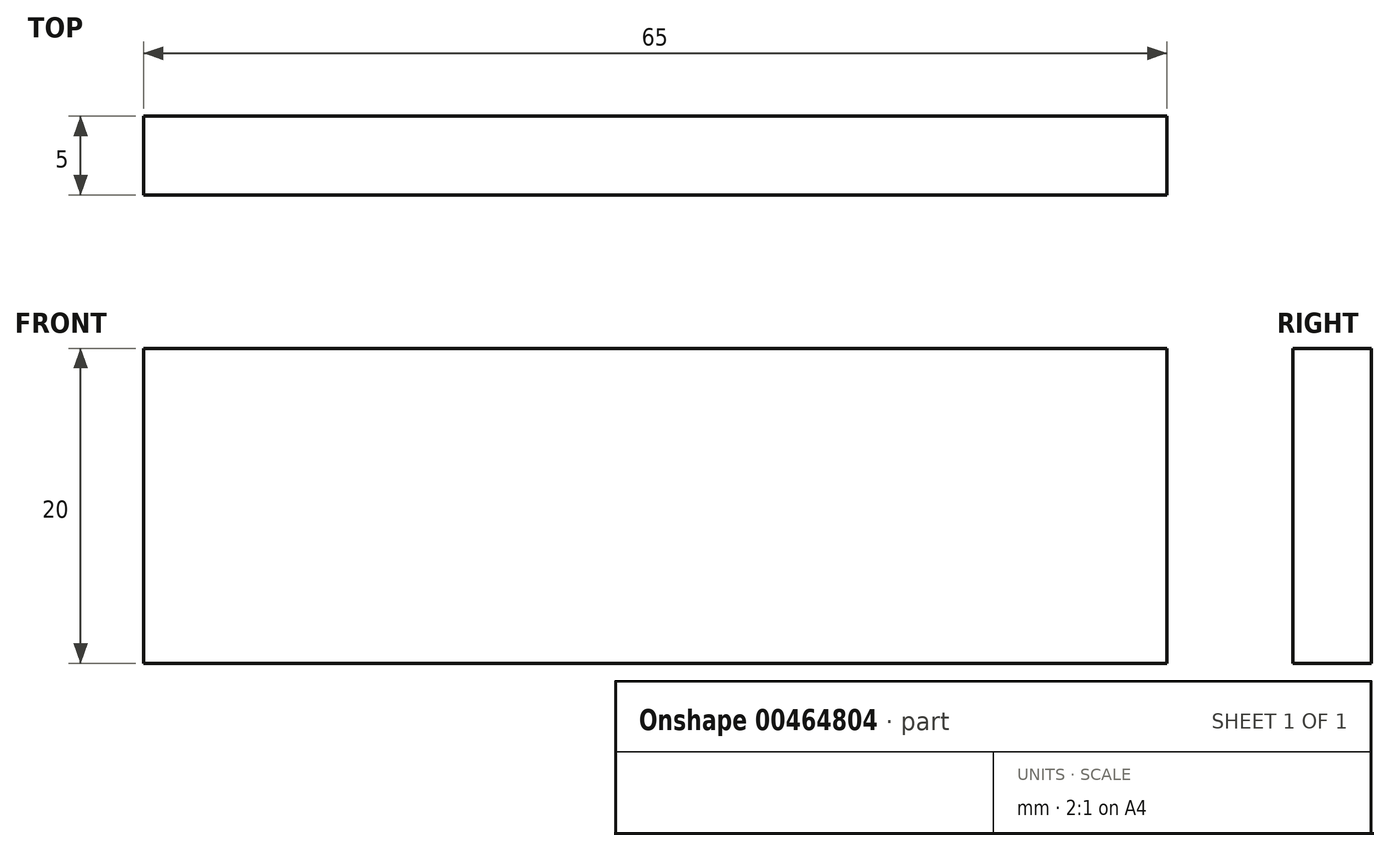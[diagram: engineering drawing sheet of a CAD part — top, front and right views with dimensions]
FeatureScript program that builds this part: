
annotation { "Feature Type Name" : "Feature", "Feature Type Description" : "" }
export const myFeature = defineFeature(function(context is Context, id is Id, definition is map)
    precondition{}
    {
        {
            var Q0;
            Q0=qCreatedBy(makeId("Front.planeOp"),FACE);
            var sketch = newSketch(context, id + "F0", { "sketchPlane" : qUnion([Q0])});
            skLineSegment(sketch, "E0.bottom", {"start": v(0, 0) * mm, "end": v(65, 0) * mm});
            skLineSegment(sketch, "E0.top", {"start": v(0, 20) * mm, "end": v(65, 20) * mm});
            skLineSegment(sketch, "E0.left", {"start": v(0, 0) * mm, "end": v(0, 20) * mm});
            skLineSegment(sketch, "E0.right", {"start": v(65, 0) * mm, "end": v(65, 20) * mm});
            skSolve(sketch);
        }
        {
            var Q0;
            Q0 = qSketchRegion(id + "F0", true);
            extrude(context, id + "F1", {"entities" : qUnion([Q0]), "depth" : 5 * mm});
        }
    });
